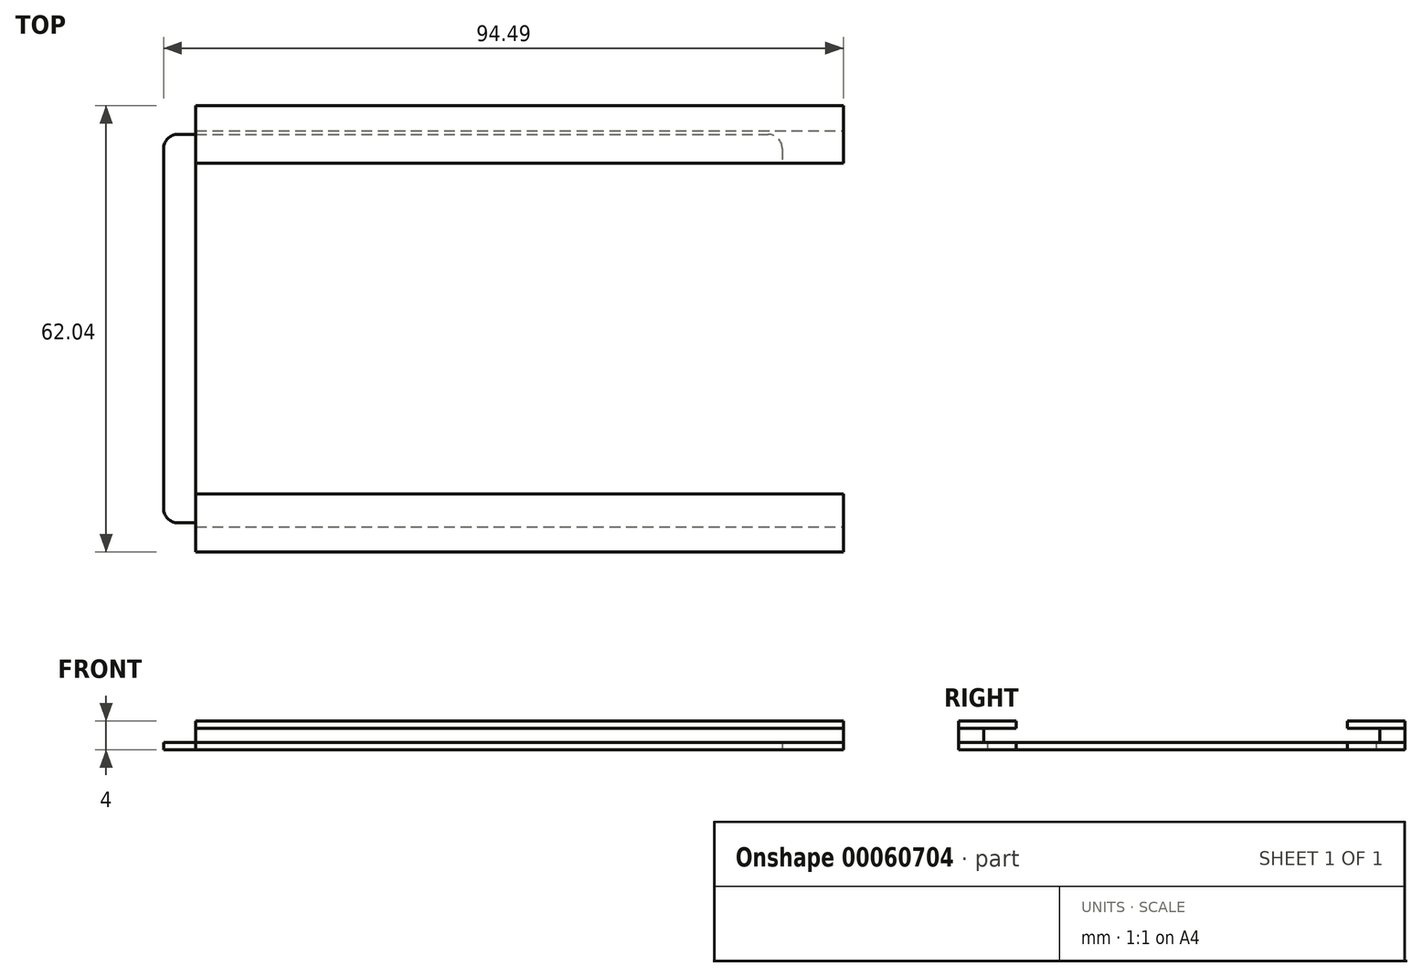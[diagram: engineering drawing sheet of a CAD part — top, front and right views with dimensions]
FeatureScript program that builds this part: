
annotation { "Feature Type Name" : "Feature", "Feature Type Description" : "" }
export const myFeature = defineFeature(function(context is Context, id is Id, definition is map)
    precondition{}
    {
        {
            var Q0;
            Q0=qCreatedBy(makeId("Top.planeOp"),FACE);
            var sketch = newSketch(context, id + "F0", { "sketchPlane" : qUnion([Q0])});
            skLineSegment(sketch, "E0.bottom", {"start": v(-77.63, 0.21) * mm, "end": v(4.37, 0.21) * mm});
            skLineSegment(sketch, "E0.top", {"start": v(-77.63, -53.79) * mm, "end": v(4.37, -53.79) * mm});
            skLineSegment(sketch, "E0.left", {"start": v(-79.63, -1.79) * mm, "end": v(-79.63, -51.79) * mm});
            skLineSegment(sketch, "E0.right", {"start": v(6.37, -1.79) * mm, "end": v(6.37, -51.79) * mm});
            skPoint(sketch, "E1.visualSharp", {"position": v(6.37, 0.21) * mm});
            skArc(sketch, "E1.filletArc", {"start": v(6.37, -1.79) * mm, "mid": v(5.78, -0.37) * mm, "end": v(4.37, 0.21) * mm});
            skPoint(sketch, "E2.visualSharp", {"position": v(-79.63, 0.21) * mm});
            skArc(sketch, "E2.filletArc", {"start": v(-77.63, 0.21) * mm, "mid": v(-79.04, -0.37) * mm, "end": v(-79.63, -1.79) * mm});
            skPoint(sketch, "E3.visualSharp", {"position": v(6.37, -53.79) * mm});
            skArc(sketch, "E3.filletArc", {"start": v(4.37, -53.79) * mm, "mid": v(5.78, -53.2) * mm, "end": v(6.37, -51.79) * mm});
            skPoint(sketch, "E4.visualSharp", {"position": v(-79.63, -53.79) * mm});
            skArc(sketch, "E4.filletArc", {"start": v(-79.63, -51.79) * mm, "mid": v(-79.04, -53.2) * mm, "end": v(-77.63, -53.79) * mm});
            skSolve(sketch);
        }
        {
            var Q0;
            Q0=makeQuery(id+"F0.imprint","IMPRINT",FACE,{"disambiguationData":[TD([[makeQuery(id+"F0.imprint","IMPRINT",EDGE,{"derivedFrom":sQuery(id+"F0.wireOp",EDGE,"E0.bottom")}),-1.0]])]});
            var sketch = newSketch(context, id + "F1", { "sketchPlane" : qUnion([Q0])});
            skLineSegment(sketch, "E5.bottom", {"start": v(-75.14, 4.21) * mm, "end": v(14.86, 4.21) * mm});
            skLineSegment(sketch, "E5.top", {"start": v(-75.14, -3.79) * mm, "end": v(14.86, -3.79) * mm});
            skLineSegment(sketch, "E5.left", {"start": v(-75.14, 4.21) * mm, "end": v(-75.14, -3.79) * mm});
            skLineSegment(sketch, "E5.right", {"start": v(14.86, 4.21) * mm, "end": v(14.86, -3.79) * mm});
            skLineSegment(sketch, "E6.bottom", {"start": v(-75.14, -49.79) * mm, "end": v(14.86, -49.79) * mm});
            skLineSegment(sketch, "E6.top", {"start": v(-75.14, -57.79) * mm, "end": v(14.86, -57.79) * mm});
            skLineSegment(sketch, "E6.left", {"start": v(-75.14, -49.79) * mm, "end": v(-75.14, -57.79) * mm});
            skLineSegment(sketch, "E6.right", {"start": v(14.86, -49.79) * mm, "end": v(14.86, -57.79) * mm});
            skLineSegment(sketch, "E7.bottom", {"start": v(-68.81, -3.79) * mm, "end": v(6.19, -3.79) * mm});
            skLineSegment(sketch, "E7.top", {"start": v(-68.81, -49.79) * mm, "end": v(6.19, -49.79) * mm});
            skPoint(sketch, "E8.orphan", {"position": v(-68.81, -7.36) * mm});
            skPoint(sketch, "E9.trimOffspring.start.orphan", {"position": v(-34.22, -28.57) * mm});
            skLineSegment(sketch, "E10.top", {"start": v(-75.14, -49.79) * mm, "end": v(-68.81, -49.79) * mm});
            skLineSegment(sketch, "E11.top", {"start": v(6.19, -49.79) * mm, "end": v(0.46, -49.79) * mm});
            skLineSegment(sketch, "E12.bottom", {"start": v(-75.14, -3.79) * mm, "end": v(-68.81, -3.79) * mm});
            skLineSegment(sketch, "E12.left", {"start": v(-75.14, -3.79) * mm, "end": v(-75.14, -49.79) * mm});
            skLineSegment(sketch, "E12.right", {"start": v(-68.81, -3.79) * mm, "end": v(-68.81, -49.79) * mm});
            skSolve(sketch);
        }
        {
            var Q0;
            {var subQ2=sQuery(id+"F1.wireOp",EDGE,"E5.bottom");Q0=makeQuery(id+"F1.imprint","IMPRINT",FACE,{"disambiguationData":[TD([[makeQuery(id+"F1.imprint","IMPRINT",EDGE,{"derivedFrom":subQ2}),-1.0]])]});}
            var Q1;
            Q1=makeQuery(id+"F1.imprint","IMPRINT",FACE,{"disambiguationData":[TD([[makeQuery(id+"F1.imprint","IMPRINT",EDGE,{"derivedFrom":sQuery(id+"F1.wireOp",EDGE,"E6.top")}),1.0]])]});
            var Q2;
            Q2=makeQuery(id+"F1.imprint","IMPRINT",FACE,{"disambiguationData":[TD([[makeQuery(id+"F1.imprint","IMPRINT",EDGE,{"derivedFrom":makeQuery(id+"F0.imprint","IMPRINT",EDGE,{"derivedFrom":sQuery(id+"F0.wireOp",EDGE,"E0.top")})}),1.0]])]});
            var Q3;
            {var subQ0=sQuery(id+"F1.wireOp",EDGE,"BtZcOUnZ-COcb-tLaw-gwyT-mFSVAKuDpH3p");var subQ1=sQuery(id+"F1.wireOp",EDGE,"E3qmf0sL-nNix-pvWN-kWZk-dvURZ8ent4av");var subQ2=makeQuery(id+"F1.imprint","INTERSECT",VERTEX,{"derivedFrom":[subQ1,subQ0]});Q3=makeQuery(id+"F1.imprint","IMPRINT",FACE,{"disambiguationData":[TD([[makeQuery(id+"F1.imprint","IMPRINT",EDGE,{"disambiguationData":[TD([[subQ2,-1.0]])],"derivedFrom":subQ1}),-1.0]])]});}
            var Q4;
            {var subQ0=sQuery(id+"F1.wireOp",EDGE,"HiAJ7JZe-PJX3-0Q2X-Z0e7-oXujONjYhCit");Q4=makeQuery(id+"F1.imprint","IMPRINT",FACE,{"disambiguationData":[TD([[makeQuery(id+"F1.imprint","IMPRINT",EDGE,{"derivedFrom":subQ0}),1.0]])]});}
            var Q5;
            {var subQ0=sQuery(id+"F1.wireOp",EDGE,"E7.bottom");Q5=makeQuery(id+"F1.imprint","IMPRINT",FACE,{"disambiguationData":[TD([[makeQuery(id+"F1.imprint","IMPRINT",EDGE,{"derivedFrom":subQ0}),1.0]])]});}
            extrude(context, id + "F2", {"entities" : qUnion([Q0, Q1, Q2, Q3, Q4, Q5]), "depth" : 1 * mm});
        }
        {
            var Q0;
            Q0=makeQuery(id+"F2.opExtrude","CAP_FACE",FACE,{"disambiguationData":[OSD([sQuery(id+"F1.wireOp",EDGE,"E5.bottom"),sQuery(id+"F1.wireOp",EDGE,"E5.top"),sQuery(id+"F1.wireOp",EDGE,"E5.left"),sQuery(id+"F1.wireOp",EDGE,"E5.right")])],"isStart":false});
            var sketch = newSketch(context, id + "F3", { "sketchPlane" : qUnion([Q0])});
            skLineSegment(sketch, "E13.bottom", {"start": v(-75.14, 4.21) * mm, "end": v(14.86, 4.21) * mm});
            skLineSegment(sketch, "E13.top", {"start": v(-75.14, 0.71) * mm, "end": v(14.86, 0.71) * mm});
            skLineSegment(sketch, "E13.left", {"start": v(-75.14, 4.21) * mm, "end": v(-75.14, 0.71) * mm});
            skLineSegment(sketch, "E13.right", {"start": v(14.86, 4.21) * mm, "end": v(14.86, 0.71) * mm});
            skLineSegment(sketch, "E14.bottom", {"start": v(-75.14, -57.83) * mm, "end": v(14.86, -57.83) * mm});
            skLineSegment(sketch, "E14.top", {"start": v(-75.14, -54.33) * mm, "end": v(14.86, -54.33) * mm});
            skLineSegment(sketch, "E14.left", {"start": v(-75.14, -57.83) * mm, "end": v(-75.14, -54.33) * mm});
            skLineSegment(sketch, "E14.right", {"start": v(14.86, -57.83) * mm, "end": v(14.86, -54.33) * mm});
            skSolve(sketch);
        }
        {
            var Q0;
            Q0=makeQuery(id+"F3.imprint","IMPRINT",FACE,{"disambiguationData":[TD([[makeQuery(id+"F3.imprint","IMPRINT",EDGE,{"derivedFrom":sQuery(id+"F3.wireOp",EDGE,"E13.bottom")}),-1.0]])]});
            var Q1;
            Q1=makeQuery(id+"F3.imprint","IMPRINT",FACE,{"disambiguationData":[TD([[makeQuery(id+"F3.imprint","IMPRINT",EDGE,{"derivedFrom":sQuery(id+"F3.wireOp",EDGE,"E14.bottom")}),1.0]])]});
            var Q2;
            {var subQ0=sQuery(id+"F3.wireOp",EDGE,"E14.top");Q2=makeQuery(id+"F3.imprint","IMPRINT",FACE,{"disambiguationData":[TD([[makeQuery(id+"F3.imprint","IMPRINT",EDGE,{"derivedFrom":subQ0}),-1.0]])]});}
            extrude(context, id + "F4", {"entities" : qUnion([Q0, Q1, Q2]), "depth" : 2 * mm});
        }
        {
            var Q0;
            Q0=makeQuery(id+"F4.opExtrude","CAP_FACE",FACE,{"disambiguationData":[OSD([sQuery(id+"F3.wireOp",EDGE,"E13.bottom"),sQuery(id+"F3.wireOp",EDGE,"E13.top"),sQuery(id+"F3.wireOp",EDGE,"E13.left"),sQuery(id+"F3.wireOp",EDGE,"E13.right")])],"isStart":false});
            var sketch = newSketch(context, id + "F5", { "sketchPlane" : qUnion([Q0])});
            skLineSegment(sketch, "E15.bottom", {"start": v(-75.14, 4.21) * mm, "end": v(14.86, 4.21) * mm});
            skLineSegment(sketch, "E15.top", {"start": v(-75.14, -3.79) * mm, "end": v(14.86, -3.79) * mm});
            skLineSegment(sketch, "E15.left", {"start": v(-75.14, 4.21) * mm, "end": v(-75.14, -3.79) * mm});
            skLineSegment(sketch, "E15.right", {"start": v(14.86, 4.21) * mm, "end": v(14.86, -3.79) * mm});
            skLineSegment(sketch, "E16.bottom", {"start": v(14.86, -57.83) * mm, "end": v(-75.14, -57.83) * mm});
            skLineSegment(sketch, "E16.top", {"start": v(14.86, -49.79) * mm, "end": v(-75.14, -49.79) * mm});
            skLineSegment(sketch, "E16.left", {"start": v(14.86, -57.83) * mm, "end": v(14.86, -49.79) * mm});
            skLineSegment(sketch, "E16.right", {"start": v(-75.14, -57.83) * mm, "end": v(-75.14, -49.79) * mm});
            skSolve(sketch);
        }
        {
            var Q0;
            {var subQ0=sQuery(id+"F5.wireOp",EDGE,"E15.bottom");Q0=makeQuery(id+"F5.imprint","IMPRINT",FACE,{"disambiguationData":[TD([[makeQuery(id+"F5.imprint","IMPRINT",EDGE,{"derivedFrom":subQ0}),-1.0]])]});}
            var Q1;
            {var subQ0=sQuery(id+"F5.wireOp",EDGE,"E15.top");Q1=makeQuery(id+"F5.imprint","IMPRINT",FACE,{"disambiguationData":[TD([[makeQuery(id+"F5.imprint","IMPRINT",EDGE,{"derivedFrom":subQ0}),1.0]])]});}
            var Q2;
            Q2=makeQuery(id+"F5.imprint","IMPRINT",FACE,{"disambiguationData":[TD([[makeQuery(id+"F5.imprint","IMPRINT",EDGE,{"derivedFrom":sQuery(id+"F5.wireOp",EDGE,"E16.bottom")}),-1.0]])]});
            extrude(context, id + "F6", {"entities" : qUnion([Q0, Q1, Q2]), "depth" : 1 * mm});
        }
    });
